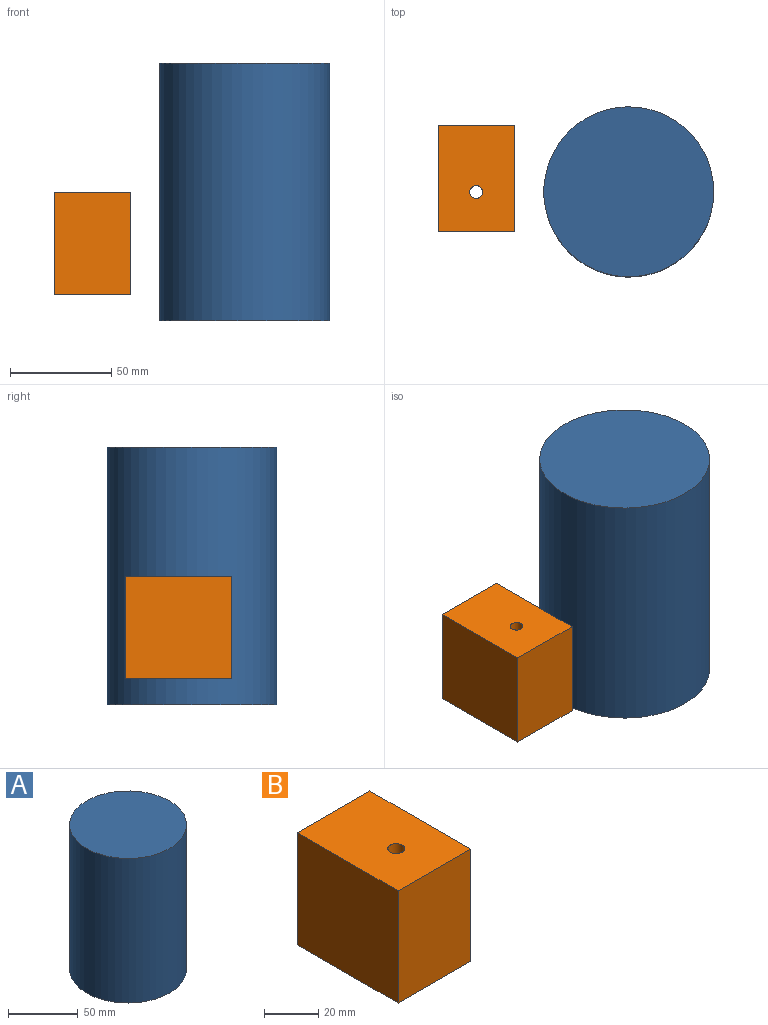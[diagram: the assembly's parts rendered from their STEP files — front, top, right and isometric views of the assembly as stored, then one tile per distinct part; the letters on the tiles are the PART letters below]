
ASSEMBLY  parts=2 mates=1
PART A: 3 faces, bbox 83.9x83.9x127 mm
  f0: cylinder r=41.96mm len=127mm, axis (0,0,-1), area 33480.1mm2, adj f1,f2
  f1: plane 83.91x83.91mm, normal (0,0,1), area 5530.4mm2, adj f0
  f2: plane 83.91x83.91mm, normal (0,0,-1), area 5530.4mm2, adj f0
PART B: 7 faces, bbox 37.8x52.6x50.8 mm
  f0: plane 50.8x37.84mm, normal (0,1,0), area 1922.2mm2, adj f1,f3,f4,f5
  f1: plane 52.6x50.8mm, normal (-1,0,0), area 2671.9mm2, adj f0,f2,f4,f5
  f2: plane 50.8x37.84mm, normal (0,-1,0), area 1922.2mm2, adj f1,f3,f4,f5
  f3: plane 52.6x50.8mm, normal (1,0,0), area 2671.9mm2, adj f0,f2,f4,f5
  f4: plane 52.6x37.84mm, normal (0,0,1), area 1958.5mm2, adj f0,f1,f2,f3,f6
  f5: plane 52.6x37.84mm, normal (0,0,-1), area 1958.5mm2, adj f0,f1,f2,f3,f6
  f6: cylinder r=3.17mm len=50.8mm, axis (0,0,1), area 1013.4mm2, adj f4,f5
PLACE A t=(158.14,128.16,29.41)mm
PLACE B t=(64.04,108.59,42.11)mm
MATE pin_slot A.f0 <-> B.f6  axis (0,0,-1) through (158.14,128.16,92.91)mm
